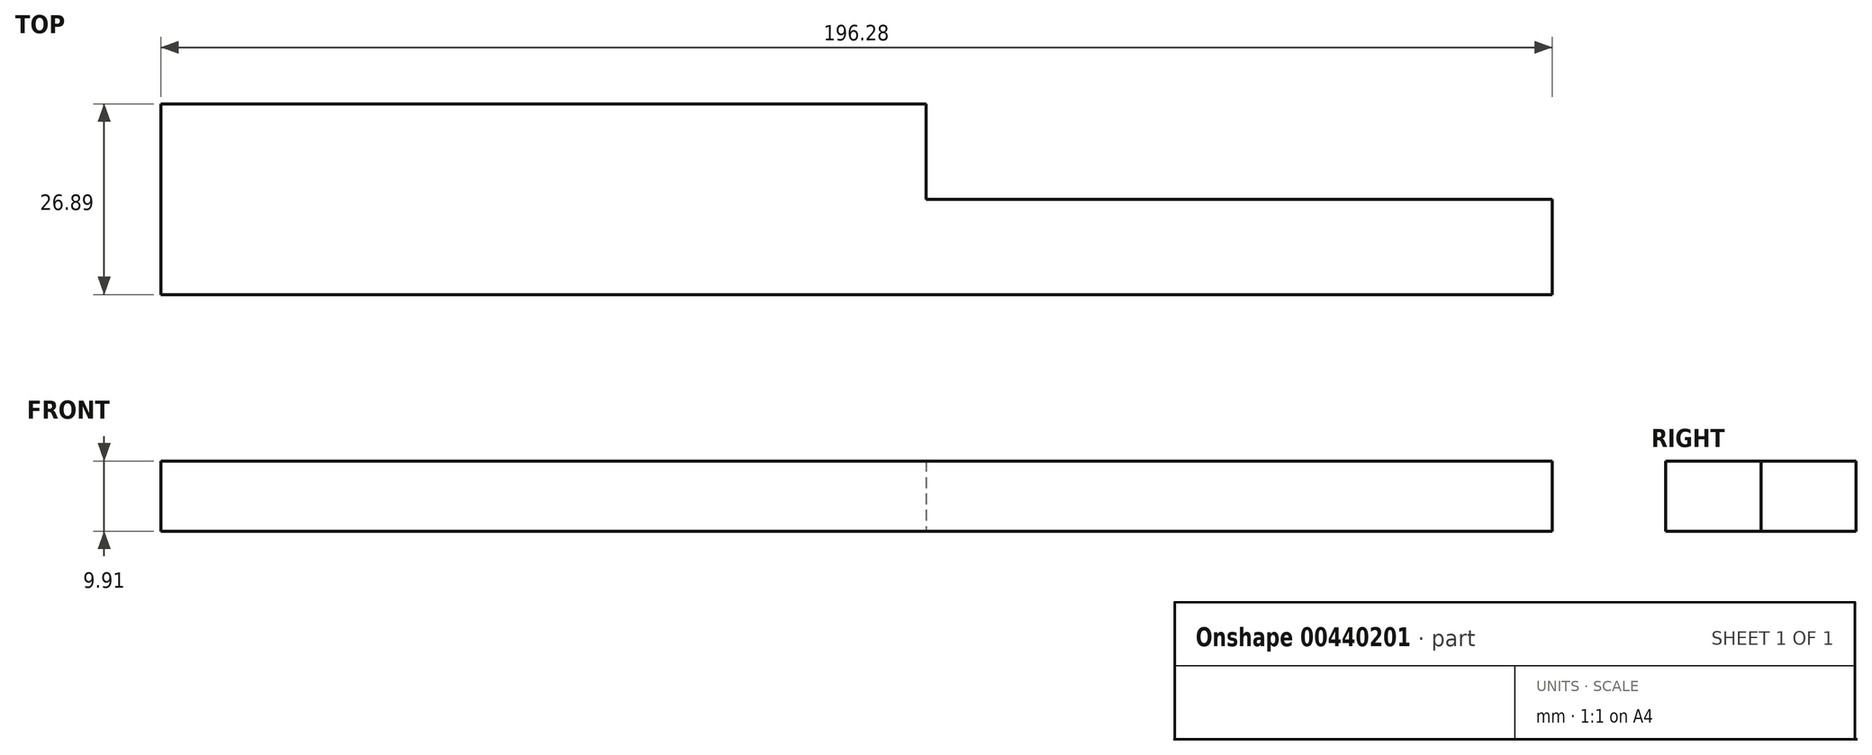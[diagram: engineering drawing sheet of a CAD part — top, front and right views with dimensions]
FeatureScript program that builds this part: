
annotation { "Feature Type Name" : "Feature", "Feature Type Description" : "" }
export const myFeature = defineFeature(function(context is Context, id is Id, definition is map)
    precondition{}
    {
        {
            var Q0;
            Q0=qCreatedBy(makeId("Top.planeOp"),FACE);
            var sketch = newSketch(context, id + "F0", { "sketchPlane" : qUnion([Q0])});
            skLineSegment(sketch, "E0.bottom", {"start": v(-87.9, -13.65) * mm, "end": v(20.05, -13.65) * mm});
            skLineSegment(sketch, "E0.top", {"start": v(-87.9, -40.54) * mm, "end": v(20.05, -40.54) * mm});
            skLineSegment(sketch, "E0.left", {"start": v(-87.9, -13.65) * mm, "end": v(-87.9, -40.54) * mm});
            skLineSegment(sketch, "E0.right", {"start": v(20.05, -13.65) * mm, "end": v(20.05, -40.54) * mm});
            skLineSegment(sketch, "E1.bottom", {"start": v(20.05, -27.1) * mm, "end": v(108.38, -27.1) * mm});
            skLineSegment(sketch, "E1.top", {"start": v(20.05, -40.54) * mm, "end": v(108.38, -40.54) * mm});
            skLineSegment(sketch, "E1.left", {"start": v(20.05, -27.1) * mm, "end": v(20.05, -40.54) * mm});
            skLineSegment(sketch, "E1.right", {"start": v(108.38, -27.1) * mm, "end": v(108.38, -40.54) * mm});
            skCircle(sketch, "E2", {"center": v(0, 0) * mm, "radius": 40.48 * mm});
            skLineSegment(sketch, "E3", {"start": v(80, -254) * mm, "end": v(80, 0) * mm, "construction": true});
            skLineSegment(sketch, "E4", {"start": v(80, 0) * mm, "end": v(0, 0) * mm, "construction": true});
            skLineSegment(sketch, "E5", {"start": v(0, 0) * mm, "end": v(-2032, 0) * mm, "construction": true});
            skSolve(sketch);
        }
        {
            var Q0;
            {var subQ0=sQuery(id+"F0.wireOp",EDGE,"E0.left");Q0=makeQuery(id+"F0.imprint","IMPRINT",FACE,{"disambiguationData":[TD([[makeQuery(id+"F0.imprint","IMPRINT",EDGE,{"derivedFrom":subQ0}),1.0]])]});}
            var Q1;
            {var subQ0=sQuery(id+"F0.wireOp",EDGE,"E1.right");Q1=makeQuery(id+"F0.imprint","IMPRINT",FACE,{"disambiguationData":[TD([[makeQuery(id+"F0.imprint","IMPRINT",EDGE,{"derivedFrom":subQ0}),-1.0]])]});}
            var Q2;
            {var subQ1=sQuery(id+"F0.wireOp",EDGE,"E0.top");var subQ3=sQuery(id+"F0.wireOp",EDGE,"E2");var subQ4=makeQuery(id+"F0.imprint","INTERSECT",VERTEX,{"derivedFrom":[subQ1,subQ3]});Q2=makeQuery(id+"F0.imprint","IMPRINT",FACE,{"disambiguationData":[TD([[makeQuery(id+"F0.imprint","IMPRINT",EDGE,{"disambiguationData":[TD([[subQ4,-1.0]])],"derivedFrom":subQ3}),1.0]])]});}
            var Q3;
            {var subQ1=sQuery(id+"F0.wireOp",EDGE,"E0.right");Q3=makeQuery(id+"F0.imprint","IMPRINT",FACE,{"disambiguationData":[TD([[makeQuery(id+"F0.imprint","IMPRINT",EDGE,{"derivedFrom":subQ1}),-1.0]])]});}
            var Q4;
            {var subQ0=sQuery(id+"F0.wireOp",EDGE,"E1.left");Q4=makeQuery(id+"F0.imprint","IMPRINT",FACE,{"disambiguationData":[TD([[makeQuery(id+"F0.imprint","IMPRINT",EDGE,{"derivedFrom":subQ0}),1.0]])]});}
            var Q5;
            {var subQ0=sQuery(id+"F0.wireOp",EDGE,"E0.right");Q5=makeQuery(id+"F0.imprint","IMPRINT",FACE,{"disambiguationData":[TD([[makeQuery(id+"F0.imprint","IMPRINT",EDGE,{"derivedFrom":subQ0}),1.0]])]});}
            extrude(context, id + "F1", {"entities" : qUnion([Q0, Q1, Q2, Q3, Q4, Q5]), "depth" : 9.9 * mm});
        }
    });
